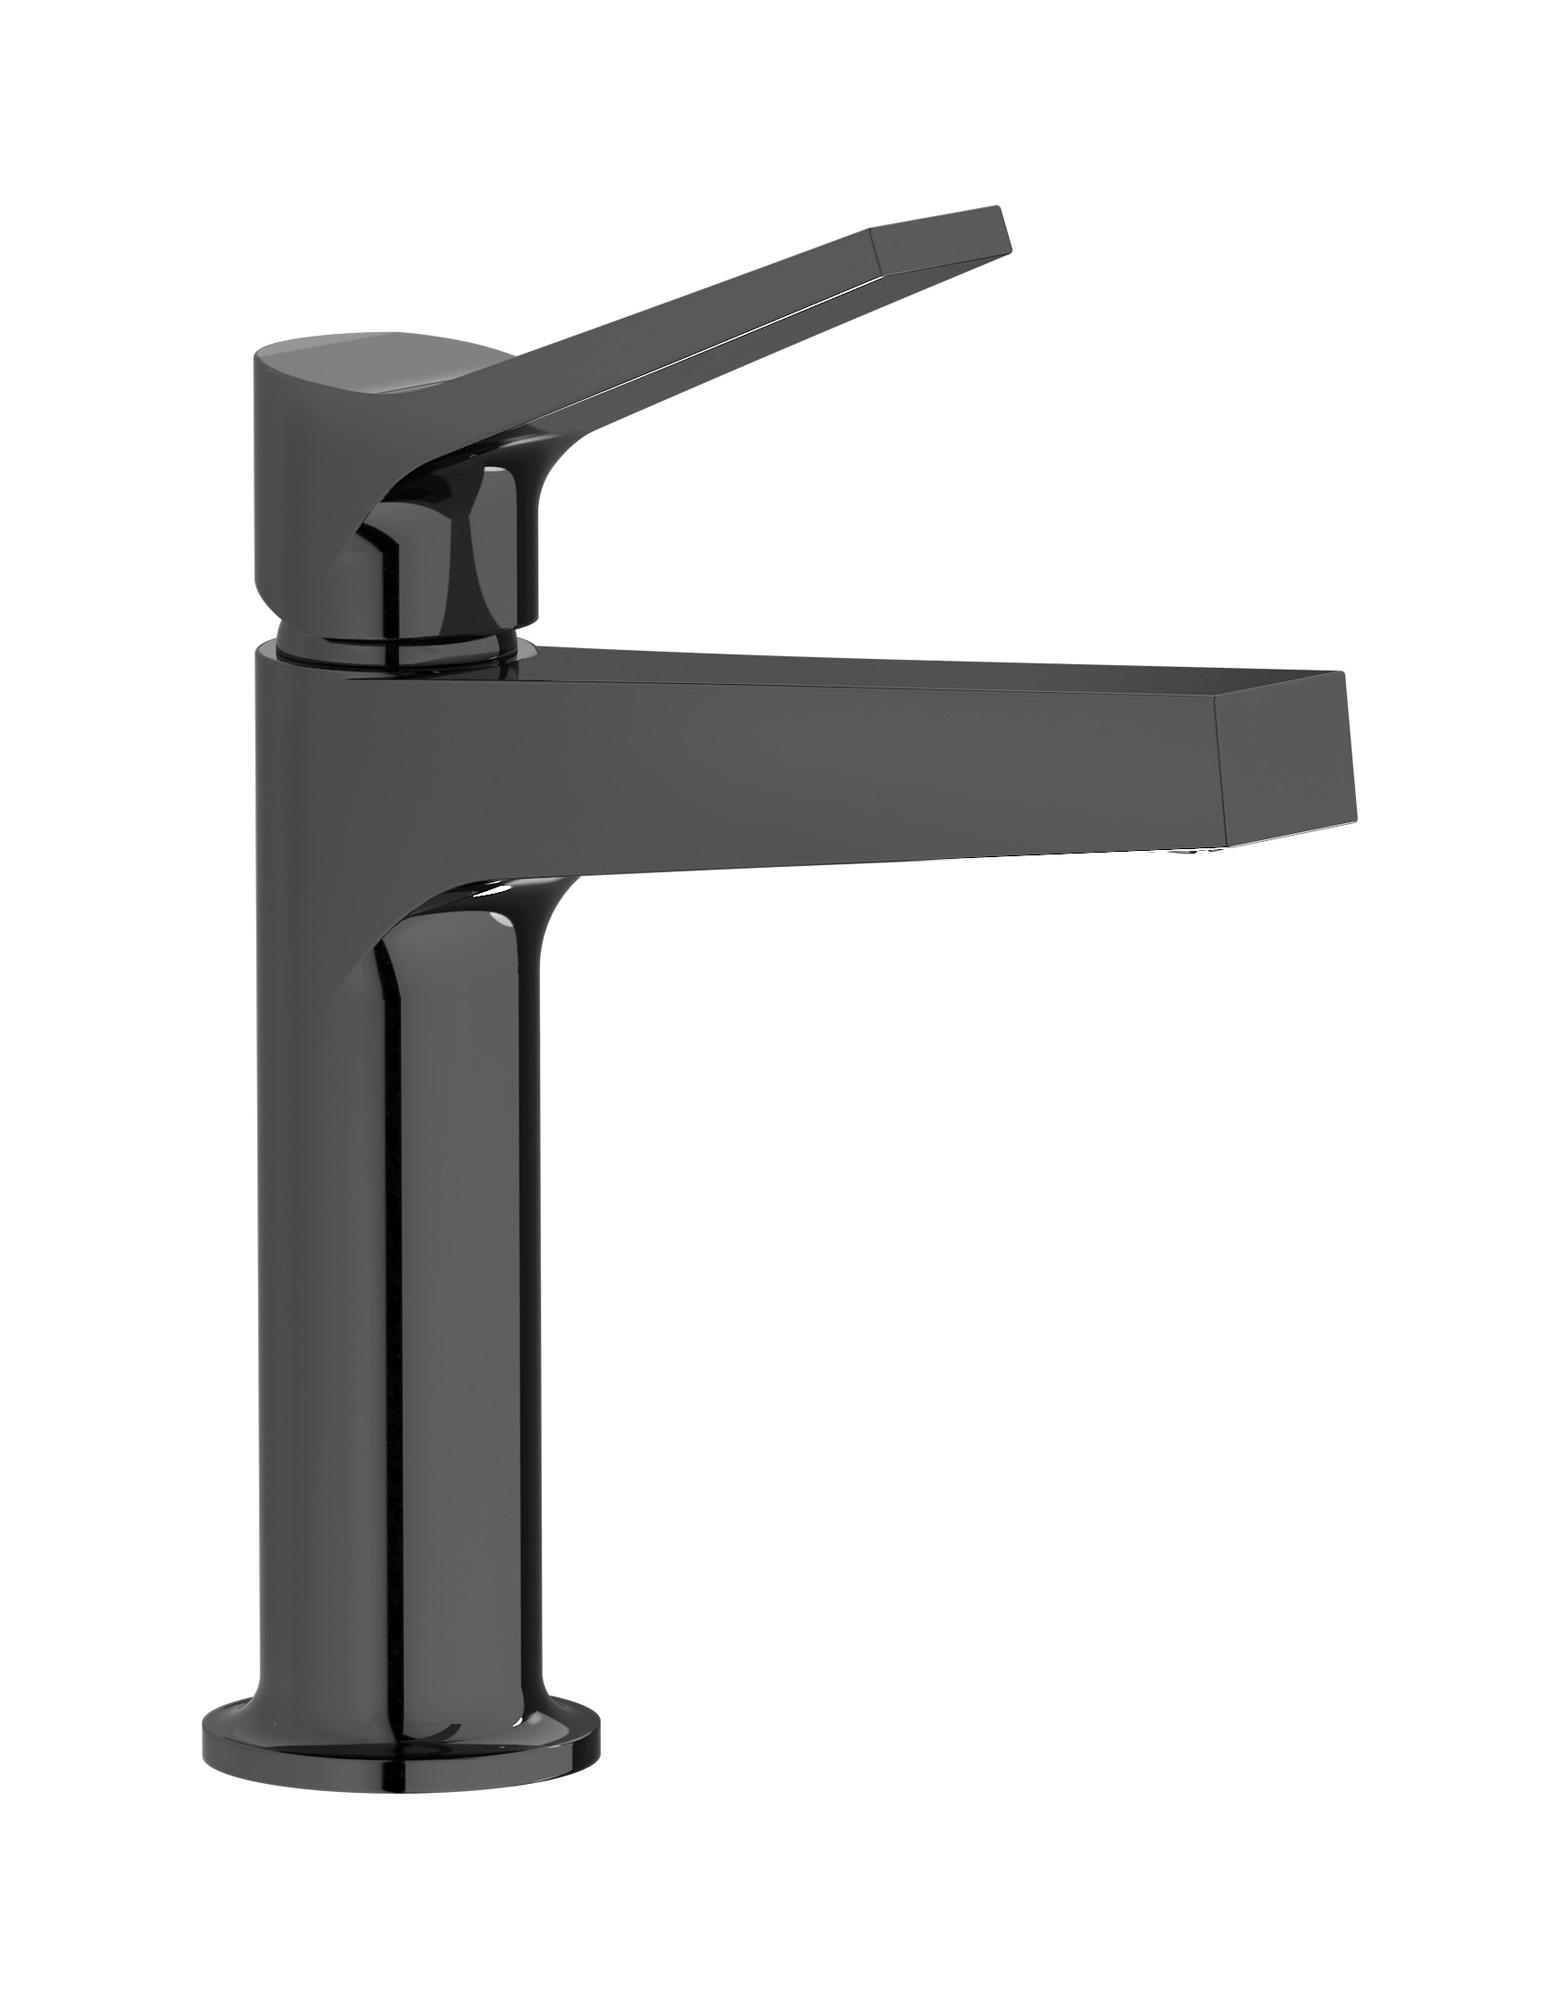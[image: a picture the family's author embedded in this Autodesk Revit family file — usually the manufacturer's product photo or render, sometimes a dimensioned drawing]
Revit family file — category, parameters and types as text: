
# Revit family: TW200
name_source: partatom
category: Apparecchi idraulici
units: mm (PartAtom-declared; Revit-internal decimal feet)

## family parameters
Basato su piano di lavoro = No
Condiviso = No
Mantieni orientamento annotazione = No
Numero OmniClass = 23.45.55.00
Punto di calcolo locali = No
Quota connettore circolare = Usa diametro
Sempre verticale = Sì
Taglio con vuoti quando caricato = No
Tipo di parte = Normale
Titolo OmniClass = Sanitary Faucets, Wastes

## types (12) — shared parameters
Cold water inlet = 10 mm  [stored 0.0328084 ft]
Commenti sul tipo = Washbasin mixer
Connessione CW = No
Connessione HW = No
Connessione di scarico = No
Connessione di ventilazione = No
Descrizione = Monohole washbasin mixer complete with drain
Hot water inlet = 10 mm  [stored 0.0328084 ft]
Produttore = IB Rubinetterie S.p.A.
URL = https://www.weareib.it
zero-valued in all types: Prospetto di default

## per-type parameters (varying)
| type | Finishes surface | Immagine tipo | Modello |
| Chrome | IB_Chrome | TW200CC.jpg | TW200CC |
| Matt white | IB_matt white | TW200BO.jpg | TW200BO |
| Matt black | IB_matt black | TW200NP.jpg | TW200NP |
| Black chrome | IB_Black chrome | TW200CF.jpg | TW200CF |
| Brushed nickel | IB_Brushed nickel | TW200SS.jpg | TW200SS |
| Brushed black chrome | IB_Brushed black chrome | TW200CS.jpg | TW200CS |
| Pale gold | IB_Pale gold | TW200II.jpg | TW200II |
| Brushed pale gold | IB_brushed pale gold | TW200IS.jpg | TW200IS |
| Rose gold | IB_Rose gold | TW200RS.jpg | TW200RS |
| Brushed rose gold | IB_Brushed rose gold | TW200SR.jpg | TW200SR |
| Gold | IB_gold | TW200OO.jpg | TW200OO |
| Brushed gold | IB_brushed gold | TW200OS.jpg | TW200OS |

note: [stored X ft] marks values corroborated as IEEE doubles in the binary element streams (Revit-internal decimal feet)
